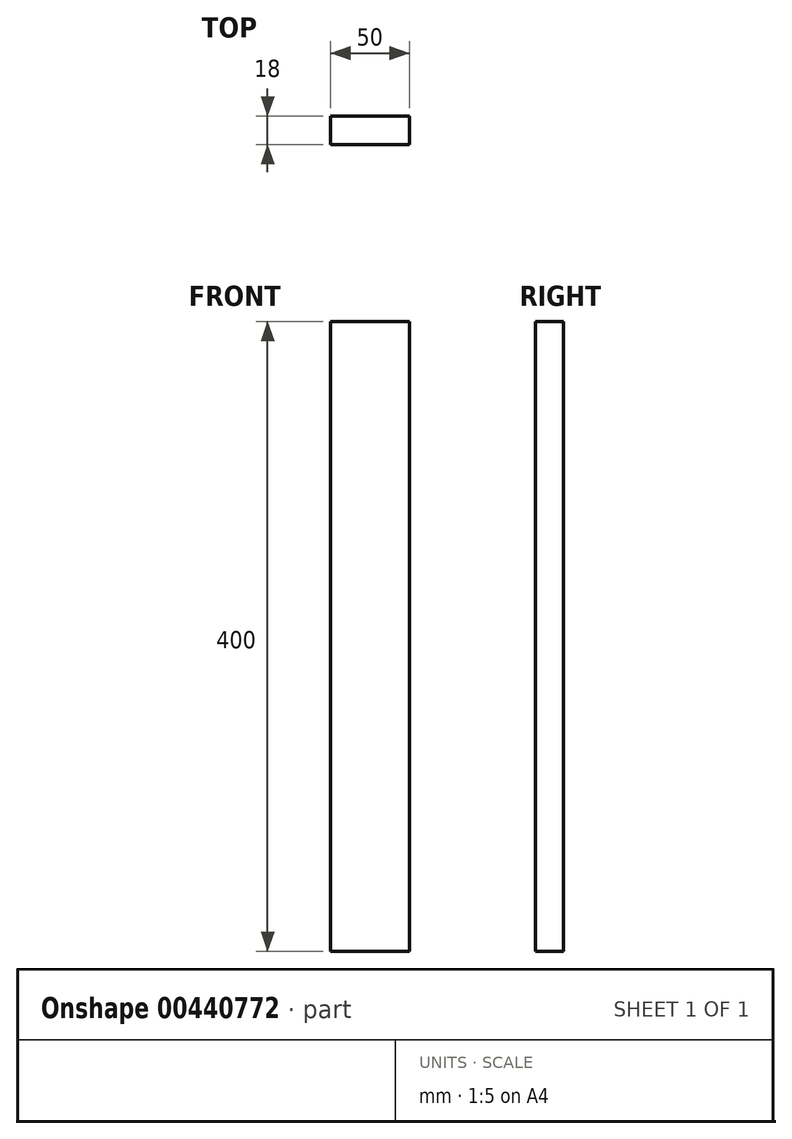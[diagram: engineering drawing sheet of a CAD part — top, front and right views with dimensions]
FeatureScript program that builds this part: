
annotation { "Feature Type Name" : "Feature", "Feature Type Description" : "" }
export const myFeature = defineFeature(function(context is Context, id is Id, definition is map)
    precondition{}
    {
        {
            var Q0;
            Q0=qCreatedBy(makeId("Top.planeOp"),FACE);
            var sketch = newSketch(context, id + "F0", { "sketchPlane" : qUnion([Q0])});
            skLineSegment(sketch, "E0.bottom", {"start": v(-50, 18) * mm, "end": v(0, 18) * mm});
            skLineSegment(sketch, "E0.top", {"start": v(-50, 0) * mm, "end": v(0, 0) * mm});
            skLineSegment(sketch, "E0.left", {"start": v(-50, 18) * mm, "end": v(-50, 0) * mm});
            skLineSegment(sketch, "E0.right", {"start": v(0, 18) * mm, "end": v(0, 0) * mm});
            skSolve(sketch);
        }
        {
            var Q0;
            Q0 = qSketchRegion(id + "F0", true);
            extrude(context, id + "F1", {"entities" : qUnion([Q0]), "depth" : 400 * mm});
        }
    });
